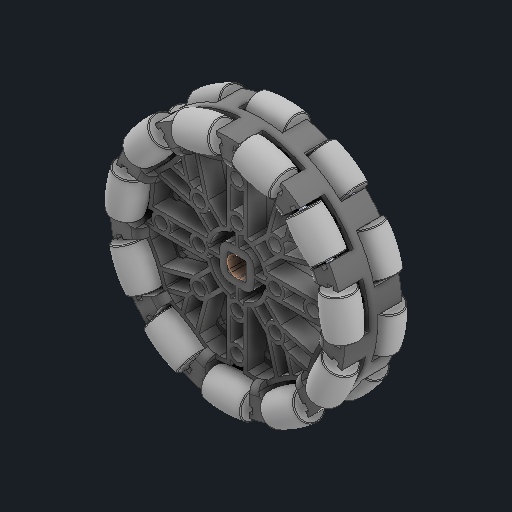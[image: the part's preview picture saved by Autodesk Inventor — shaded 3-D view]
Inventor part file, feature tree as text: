
AUTODESK INVENTOR PART (.ipt)
format: ipt  version: 2024 (Build 280153000, 153)  size: 3,338,752 bytes
history: native  units: in
note: dims shown in document units (in); Inventor stores cm internally (conversion verified against a paired STEP export)
features: other x49, sketch x1
ambient origin geometry x8: Origin, YZ Plane, XZ Plane, XY Plane, X Axis, Y Axis, Z Axis, Center Point
bodies: Solid1 (feature_tree), Solid2 (feature_tree), Solid3 (feature_tree), Solid4 (feature_tree), Solid5 (feature_tree), Solid6 (feature_tree), Solid7 (feature_tree), Solid8 (feature_tree), Solid9 (feature_tree), Solid10 (feature_tree), Solid11 (feature_tree), Solid12 (feature_tree), Solid13 (feature_tree), Solid14 (feature_tree), Solid15 (feature_tree), Solid16 (feature_tree), Solid17 (feature_tree), Solid18 (feature_tree), Solid19 (feature_tree), Solid20 (feature_tree), Solid21 (feature_tree), Solid22 (feature_tree), Solid23 (feature_tree), Solid24 (feature_tree), Solid25 (feature_tree), Solid26 (feature_tree), Solid27 (feature_tree), Solid28 (feature_tree), Solid29 (feature_tree), Solid30 (feature_tree), Solid31 (feature_tree), Solid32 (feature_tree), Solid33 (feature_tree), Solid34 (feature_tree), Solid35 (feature_tree), Solid36 (feature_tree), Solid37 (feature_tree), Solid38 (feature_tree), Solid39 (feature_tree), Solid40 (feature_tree), Solid41 (feature_tree), Solid42 (feature_tree), Solid43 (feature_tree), Solid44 (feature_tree), Solid45 (feature_tree)
feature tree (50):
  other  "3.25 Omni Antistatic.ipt"
  other  "Solid1::3.25 Omni Antistatic.ipt"
  other  "Solid2::3.25 Omni Antistatic.ipt"
  other  "Solid3::3.25 Omni Antistatic.ipt"
  other  "Solid4::3.25 Omni Antistatic.ipt"
  other  "Solid5::3.25 Omni Antistatic.ipt"
  other  "Solid6::3.25 Omni Antistatic.ipt"
  other  "Solid7::3.25 Omni Antistatic.ipt"
  other  "Solid8::3.25 Omni Antistatic.ipt"
  other  "Solid9::3.25 Omni Antistatic.ipt"
  other  "Solid10::3.25 Omni Antistatic.ipt"
  other  "Solid11::3.25 Omni Antistatic.ipt"
  other  "Solid12::3.25 Omni Antistatic.ipt"
  other  "Solid13::3.25 Omni Antistatic.ipt"
  other  "Solid14::3.25 Omni Antistatic.ipt"
  other  "Solid15::3.25 Omni Antistatic.ipt"
  other  "Solid16::3.25 Omni Antistatic.ipt"
  other  "Solid17::3.25 Omni Antistatic.ipt"
  other  "Solid18::3.25 Omni Antistatic.ipt"
  other  "Solid19::3.25 Omni Antistatic.ipt"
  other  "Solid20::3.25 Omni Antistatic.ipt"
  other  "Solid21::3.25 Omni Antistatic.ipt"
  other  "Solid22::3.25 Omni Antistatic.ipt"
  other  "Solid23::3.25 Omni Antistatic.ipt"
  other  "Solid24::3.25 Omni Antistatic.ipt"
  other  "Solid25::3.25 Omni Antistatic.ipt"
  other  "Solid26::3.25 Omni Antistatic.ipt"
  other  "Solid27::3.25 Omni Antistatic.ipt"
  other  "Solid28::3.25 Omni Antistatic.ipt"
  other  "Solid29::3.25 Omni Antistatic.ipt"
  other  "Solid30::3.25 Omni Antistatic.ipt"
  other  "Solid31::3.25 Omni Antistatic.ipt"
  other  "Solid32::3.25 Omni Antistatic.ipt"
  other  "Solid33::3.25 Omni Antistatic.ipt"
  other  "Solid34::3.25 Omni Antistatic.ipt"
  other  "Solid35::3.25 Omni Antistatic.ipt"
  other  "Solid36::3.25 Omni Antistatic.ipt"
  other  "Solid37::3.25 Omni Antistatic.ipt"
  other  "Solid38::3.25 Omni Antistatic.ipt"
  other  "Solid39::3.25 Omni Antistatic.ipt"
  other  "Solid40::3.25 Omni Antistatic.ipt"
  other  "Solid41::3.25 Omni Antistatic.ipt"
  other  "Solid42::3.25 Omni Antistatic.ipt"
  other  "Solid43::3.25 Omni Antistatic.ipt"
  other  "Solid44::3.25 Omni Antistatic.ipt"
  other  "Solid45::3.25 Omni Antistatic.ipt"
  other  "TaggingFeature1"
  sketch  "Sketch1"  dims[d0=0.3937in]
  other  "Srf1"
  other  "Srf1::Derived"
